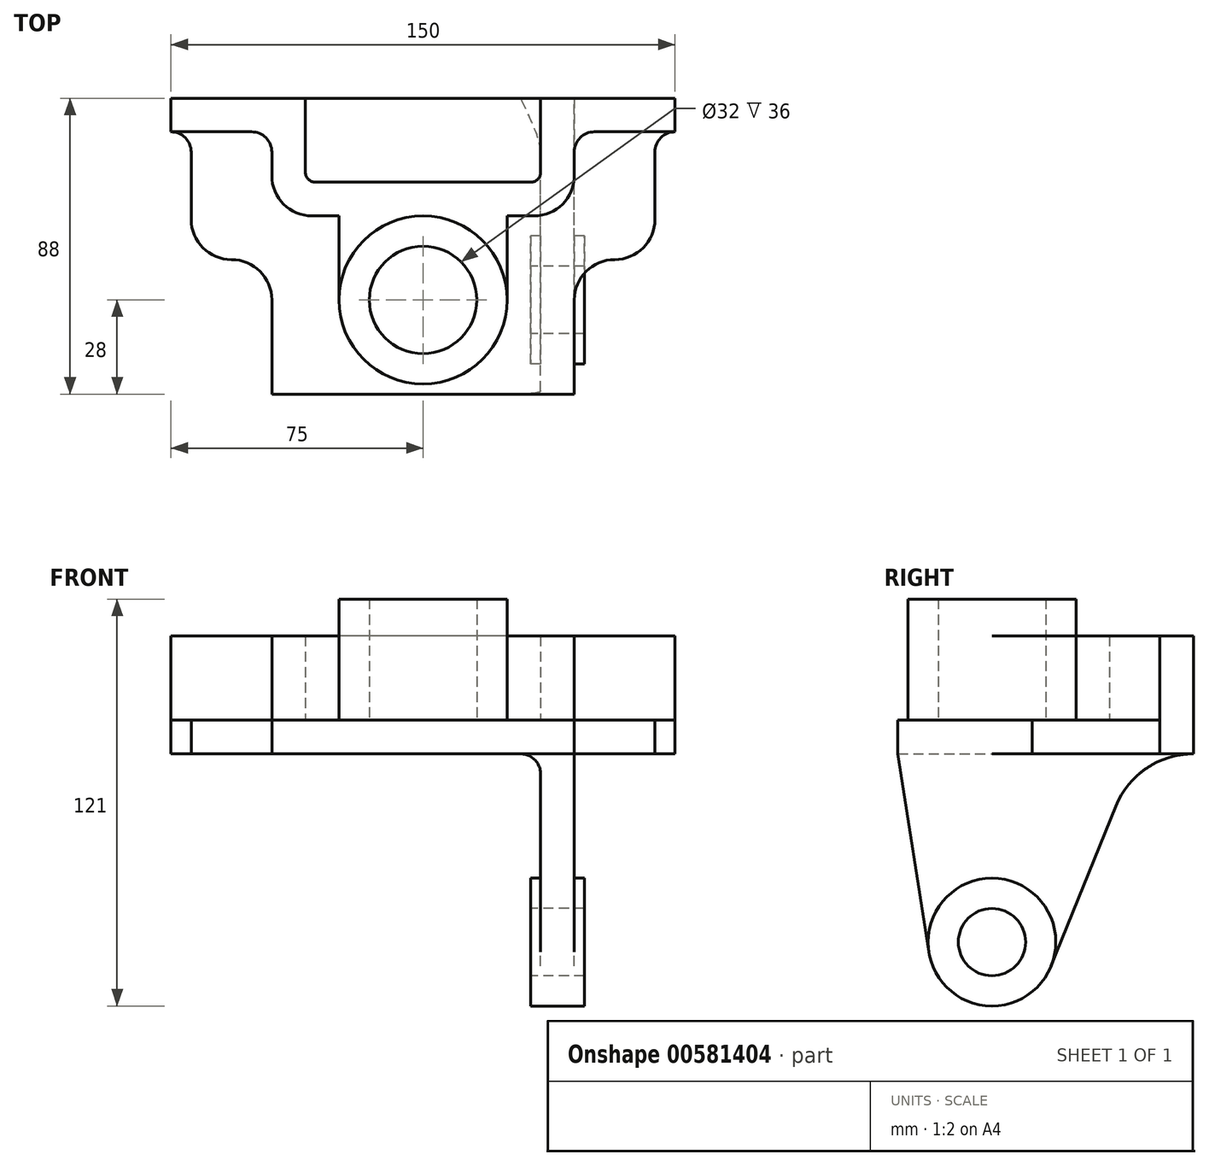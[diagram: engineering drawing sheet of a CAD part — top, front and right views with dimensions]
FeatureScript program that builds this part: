
annotation { "Feature Type Name" : "Feature", "Feature Type Description" : "" }
export const myFeature = defineFeature(function(context is Context, id is Id, definition is map)
    precondition{}
    {
        {
            var Q0;
            Q0=qCreatedBy(makeId("Top.planeOp"),FACE);
            var sketch = newSketch(context, id + "F0", { "sketchPlane" : qUnion([Q0])});
            skLineSegment(sketch, "E0.bottom", {"start": v(-75, 44) * mm, "end": v(-35, 44) * mm});
            skLineSegment(sketch, "E0.top", {"start": v(-75, -44) * mm, "end": v(75, -44) * mm});
            skLineSegment(sketch, "E0.left", {"start": v(-75, 44) * mm, "end": v(-75, -44) * mm});
            skLineSegment(sketch, "E0.right", {"start": v(75, 44) * mm, "end": v(75, -44) * mm});
            skPoint(sketch, "E0.middle", {"position": v(0, 0) * mm});
            skLineSegment(sketch, "E1.top", {"start": v(-75, 34) * mm, "end": v(-51, 34) * mm});
            skLineSegment(sketch, "E1.left", {"start": v(-75, 44) * mm, "end": v(-75, 34) * mm});
            skLineSegment(sketch, "E1.right", {"start": v(-35, 44) * mm, "end": v(-35, 34) * mm});
            skLineSegment(sketch, "E2.bottom", {"start": v(75, 44) * mm, "end": v(35, 44) * mm});
            skLineSegment(sketch, "E2.top", {"start": v(75, 34) * mm, "end": v(51, 34) * mm});
            skLineSegment(sketch, "E2.left", {"start": v(75, 44) * mm, "end": v(75, 34) * mm});
            skLineSegment(sketch, "E2.right", {"start": v(35, 44) * mm, "end": v(35, 34) * mm});
            skLineSegment(sketch, "E3.top", {"start": v(32, 19) * mm, "end": v(-32, 19) * mm});
            skLineSegment(sketch, "E3.left", {"start": v(35, 44) * mm, "end": v(35, 22) * mm});
            skLineSegment(sketch, "E3.right", {"start": v(-35, 44) * mm, "end": v(-35, 22) * mm});
            skLineSegment(sketch, "E4.0", {"start": v(-45, 28) * mm, "end": v(-45, 21) * mm});
            skLineSegment(sketch, "E5.0", {"start": v(45, 28) * mm, "end": v(45, 21) * mm});
            skLineSegment(sketch, "E6.0", {"start": v(33, 9) * mm, "end": v(25, 9) * mm});
            skLineSegment(sketch, "E7.trimOffspring", {"start": v(35, 44) * mm, "end": v(75, 44) * mm});
            skPoint(sketch, "E8.visualSharp", {"position": v(45, 9) * mm});
            skArc(sketch, "E8.filletArc", {"start": v(33, 9) * mm, "mid": v(41.49, 12.51) * mm, "end": v(45, 21) * mm});
            skPoint(sketch, "E9.visualSharp", {"position": v(-45, 9) * mm});
            skArc(sketch, "E9.filletArc", {"start": v(-45, 21) * mm, "mid": v(-41.49, 12.51) * mm, "end": v(-33, 9) * mm});
            skPoint(sketch, "E10.visualSharp", {"position": v(45, 34) * mm});
            skArc(sketch, "E10.filletArc", {"start": v(51, 34) * mm, "mid": v(46.76, 32.24) * mm, "end": v(45, 28) * mm});
            skPoint(sketch, "E11.visualSharp", {"position": v(-45, 34) * mm});
            skArc(sketch, "E11.filletArc", {"start": v(-45, 28) * mm, "mid": v(-46.76, 32.24) * mm, "end": v(-51, 34) * mm});
            skPoint(sketch, "E12.visualSharp", {"position": v(35, 19) * mm});
            skArc(sketch, "E12.filletArc", {"start": v(32, 19) * mm, "mid": v(34.12, 19.88) * mm, "end": v(35, 22) * mm});
            skPoint(sketch, "E13.visualSharp", {"position": v(-35, 19) * mm});
            skArc(sketch, "E13.filletArc", {"start": v(-35, 22) * mm, "mid": v(-34.12, 19.88) * mm, "end": v(-32, 19) * mm});
            skCircle(sketch, "E14", {"center": v(0, -16) * mm, "radius": 25 * mm});
            skCircle(sketch, "E15", {"center": v(0, -16) * mm, "radius": 16 * mm});
            skLineSegment(sketch, "E16", {"start": v(0, -80.13) * mm, "end": v(0, 82.5) * mm, "construction": true});
            skPoint(sketch, "E16.startSnap0", {"position": v(0, -44) * mm});
            skLineSegment(sketch, "E17", {"start": v(-136.6, 0) * mm, "end": v(124.95, 0) * mm, "construction": true});
            skLineSegment(sketch, "E18", {"start": v(-35, 44) * mm, "end": v(35, 44) * mm, "construction": true});
            skPoint(sketch, "E19", {"position": v(0, 44) * mm});
            skLineSegment(sketch, "E20", {"start": v(-25, -16) * mm, "end": v(-25, 9) * mm});
            skLineSegment(sketch, "E21", {"start": v(25, -16) * mm, "end": v(25, 9) * mm});
            skLineSegment(sketch, "E22.trimOffspring", {"start": v(-25, 9) * mm, "end": v(-33, 9) * mm});
            skSolve(sketch);
        }
        {
            var Q0;
            {var subQ1=sQuery(id+"F0.wireOp",EDGE,"E0.bottom");Q0=makeQuery(id+"F0.imprint","IMPRINT",FACE,{"disambiguationData":[TD([[makeQuery(id+"F0.imprint","IMPRINT",EDGE,{"derivedFrom":subQ1}),-1.0]])]});}
            extrude(context, id + "F1", {"entities" : qUnion([Q0]), "depth" : 25 * mm, "offsetDistance" : 25 * mm});
        }
        {
            var Q0;
            Q0=makeQuery(id+"F0.imprint","IMPRINT",FACE,{"disambiguationData":[TD([[makeQuery(id+"F0.imprint","IMPRINT",EDGE,{"derivedFrom":sQuery(id+"F0.wireOp",EDGE,"E15")}),-1.0]])]});
            extrude(context, id + "F2", {"entities" : qUnion([Q0]), "operationType" : NewBodyOperationType.ADD, "depth" : 36 * mm, "offsetDistance" : 25 * mm});
        }
        {
            var Q0;
            {var subQ1=sQuery(id+"F0.wireOp",EDGE,"E0.bottom");Q0=makeQuery(id+"F0.imprint","IMPRINT",FACE,{"disambiguationData":[TD([[makeQuery(id+"F0.imprint","IMPRINT",EDGE,{"derivedFrom":subQ1}),-1.0]])]});}
            var sketch = newSketch(context, id + "F3", { "sketchPlane" : qUnion([Q0])});
            skLineSegment(sketch, "E23.bottom", {"start": v(75, 44) * mm, "end": v(-75, 44) * mm});
            skLineSegment(sketch, "E23.top", {"start": v(45, -44) * mm, "end": v(-45, -44) * mm});
            skLineSegment(sketch, "E23.right", {"start": v(-75, 44) * mm, "end": v(-75, 34) * mm});
            skPoint(sketch, "E23.middle", {"position": v(0, 0) * mm});
            skPoint(sketch, "E24", {"position": v(-45, -44) * mm});
            skPoint(sketch, "E25.0", {"position": v(0, -16) * mm});
            skLineSegment(sketch, "E26", {"start": v(45, -16) * mm, "end": v(-45, -16) * mm, "construction": true});
            skLineSegment(sketch, "E27", {"start": v(-45, -44) * mm, "end": v(-45, -16) * mm});
            skLineSegment(sketch, "E28.0.8", {"start": v(-45, -44) * mm, "end": v(45, -44) * mm});
            skLineSegment(sketch, "E29", {"start": v(-69, 8) * mm, "end": v(-69, 28) * mm});
            skArc(sketch, "E30", {"start": v(-69, 28) * mm, "mid": v(-70.76, 32.24) * mm, "end": v(-75, 34) * mm});
            skLineSegment(sketch, "E31", {"start": v(0, -44) * mm, "end": v(0, 0) * mm, "construction": true});
            skArc(sketch, "E32.MirrorCS", {"start": v(69, 28) * mm, "mid": v(70.76, 32.24) * mm, "end": v(75, 34) * mm});
            skLineSegment(sketch, "E33.MirrorCS", {"start": v(69, 8) * mm, "end": v(69, 28) * mm});
            skLineSegment(sketch, "E34.MirrorCS", {"start": v(45, -44) * mm, "end": v(45, -16) * mm});
            skLineSegment(sketch, "E35", {"start": v(75, 34) * mm, "end": v(75, 44) * mm});
            skPoint(sketch, "E28.0.10.start.orphan", {"position": v(75, 34) * mm});
            skLineSegment(sketch, "E36", {"start": v(57, -4) * mm, "end": v(57, -4) * mm});
            skArc(sketch, "E37.filletArc", {"start": v(57, -4) * mm, "mid": v(48.51, -7.51) * mm, "end": v(45, -16) * mm});
            skArc(sketch, "E38.filletArc", {"start": v(57, -4) * mm, "mid": v(65.49, -0.49) * mm, "end": v(69, 8) * mm});
            skArc(sketch, "E39.MirrorCS", {"start": v(-57, -4) * mm, "mid": v(-48.51, -7.51) * mm, "end": v(-45, -16) * mm});
            skArc(sketch, "E40.MirrorCS", {"start": v(-57, -4) * mm, "mid": v(-65.49, -0.49) * mm, "end": v(-69, 8) * mm});
            skSolve(sketch);
        }
        {
            var Q0;
            Q0 = qSketchRegion(id + "F3", true);
            extrude(context, id + "F4", {"entities" : qUnion([Q0]), "operationType" : NewBodyOperationType.ADD, "oppositeDirection" : true, "depth" : 10 * mm, "offsetDistance" : 25 * mm});
        }
        {
            var Q0;
            Q0=makeQuery(id+"F4.opExtrude","SWEPT_FACE",FACE,{"disambiguationData":[OSD([sQuery(id+"F3.wireOp",EDGE,"E34.MirrorCS")])]});
            var sketch = newSketch(context, id + "F5", { "sketchPlane" : qUnion([Q0])});
            skCircle(sketch, "E41", {"center": v(-16, -66) * mm, "radius": 10 * mm});
            skCircle(sketch, "E42", {"center": v(-16, -66) * mm, "radius": 19 * mm});
            skLineSegment(sketch, "E43", {"start": v(-44, -10) * mm, "end": v(-34.77, -68.94) * mm});
            skArc(sketch, "E44", {"start": v(44, -10) * mm, "mid": v(30.02, -14.27) * mm, "end": v(20.82, -25.63) * mm});
            skPoint(sketch, "E45.0", {"position": v(44, -10) * mm});
            skLineSegment(sketch, "E46.0", {"start": v(44, -10) * mm, "end": v(34, -10) * mm});
            skLineSegment(sketch, "E47", {"start": v(1.61, -73.12) * mm, "end": v(20.82, -25.63) * mm});
            skLineSegment(sketch, "E48", {"start": v(-44, -10) * mm, "end": v(44, -10) * mm});
            skSolve(sketch);
        }
        {
            var Q0;
            {var subQ0=sQuery(id+"F5.wireOp",EDGE,"E43");Q0=makeQuery(id+"F5.imprint","IMPRINT",FACE,{"disambiguationData":[TD([[makeQuery(id+"F5.imprint","IMPRINT",EDGE,{"derivedFrom":subQ0}),1.0]])]});}
            extrude(context, id + "F6", {"entities" : qUnion([Q0]), "operationType" : NewBodyOperationType.ADD, "oppositeDirection" : true, "depth" : 10 * mm, "offsetDistance" : 25 * mm});
        }
        {
            var Q0;
            {var subQ0=sQuery(id+"F3.wireOp",EDGE,"E34.MirrorCS");Q0=makeQuery(id+"F6.boolean.opBoolean","MERGE",FACE,{"derivedFrom":[makeQuery(id+"F4.opExtrude","SWEPT_FACE",FACE,{"disambiguationData":[OSD([subQ0])]}),makeQuery(id+"F6.opExtrude","CAP_FACE",FACE,{"disambiguationData":[OSD([subQ0,sQuery(id+"F5.wireOp",EDGE,"E42"),sQuery(id+"F5.wireOp",EDGE,"E43"),sQuery(id+"F5.wireOp",EDGE,"BQ0Ac1ui-zuDD-CszI-pBfw-mTzvjngTd8tH")])],"isStart":true})]});}
            var Q1;
            Q1=makeQuery(id+"F6.opExtrude","CAP_FACE",FACE,{"disambiguationData":[OSD([sQuery(id+"F3.wireOp",EDGE,"E34.MirrorCS"),sQuery(id+"F5.wireOp",EDGE,"E42"),sQuery(id+"F5.wireOp",EDGE,"E43"),sQuery(id+"F5.wireOp",EDGE,"BQ0Ac1ui-zuDD-CszI-pBfw-mTzvjngTd8tH")])],"isStart":false});
            cPlane(context, id + "F7", {"entities" : qUnion([Q0, Q1]), "cplaneType" : CPlaneType.MID_PLANE, "offset" : 25 * mm, "width" : 150 * mm, "height" : 150 * mm});
        }
        {
            var Q0;
            Q0=qCreatedBy(id+"F7.planeOp",FACE);
            var sketch = newSketch(context, id + "F8", { "sketchPlane" : qUnion([Q0])});
            skCircle(sketch, "E49.0", {"center": v(-16, -66) * mm, "radius": 19 * mm});
            skCircle(sketch, "E50.0", {"center": v(-16, -66) * mm, "radius": 10 * mm});
            skSolve(sketch);
        }
        {
            var Q0;
            Q0=makeQuery(id+"F8.imprint","IMPRINT",FACE,{"disambiguationData":[TD([[makeQuery(id+"F8.imprint","IMPRINT",EDGE,{"derivedFrom":sQuery(id+"F8.wireOp",EDGE,"E49.0")}),1.0]])]});
            extrude(context, id + "F9", {"entities" : qUnion([Q0]), "operationType" : NewBodyOperationType.ADD, "endBound" : BoundingType.SYMMETRIC, "depth" : 16 * mm, "offsetDistance" : 25 * mm});
        }
        {
            var Q0;
            Q0=makeQuery(id+"F11hPOX4jgopVZY_1.1.F6.opExtrude","CAP_EDGE",EDGE,{"disambiguationData":[OSD([sQuery(id+"F5.wireOp",EDGE,"E48")])],"isStart":false});
            var Q1;
            Q1=makeQuery(id+"F6.opExtrude","CAP_EDGE",EDGE,{"disambiguationData":[OSD([sQuery(id+"F5.wireOp",EDGE,"E48")])],"isStart":false});
            fillet(context, id + "F10", {"entities" : qUnion([Q0, Q1]), "radius" : 6 * mm, "tangentPropagation" : true, "allowEdgeOverflow" : false});
        }
    });
